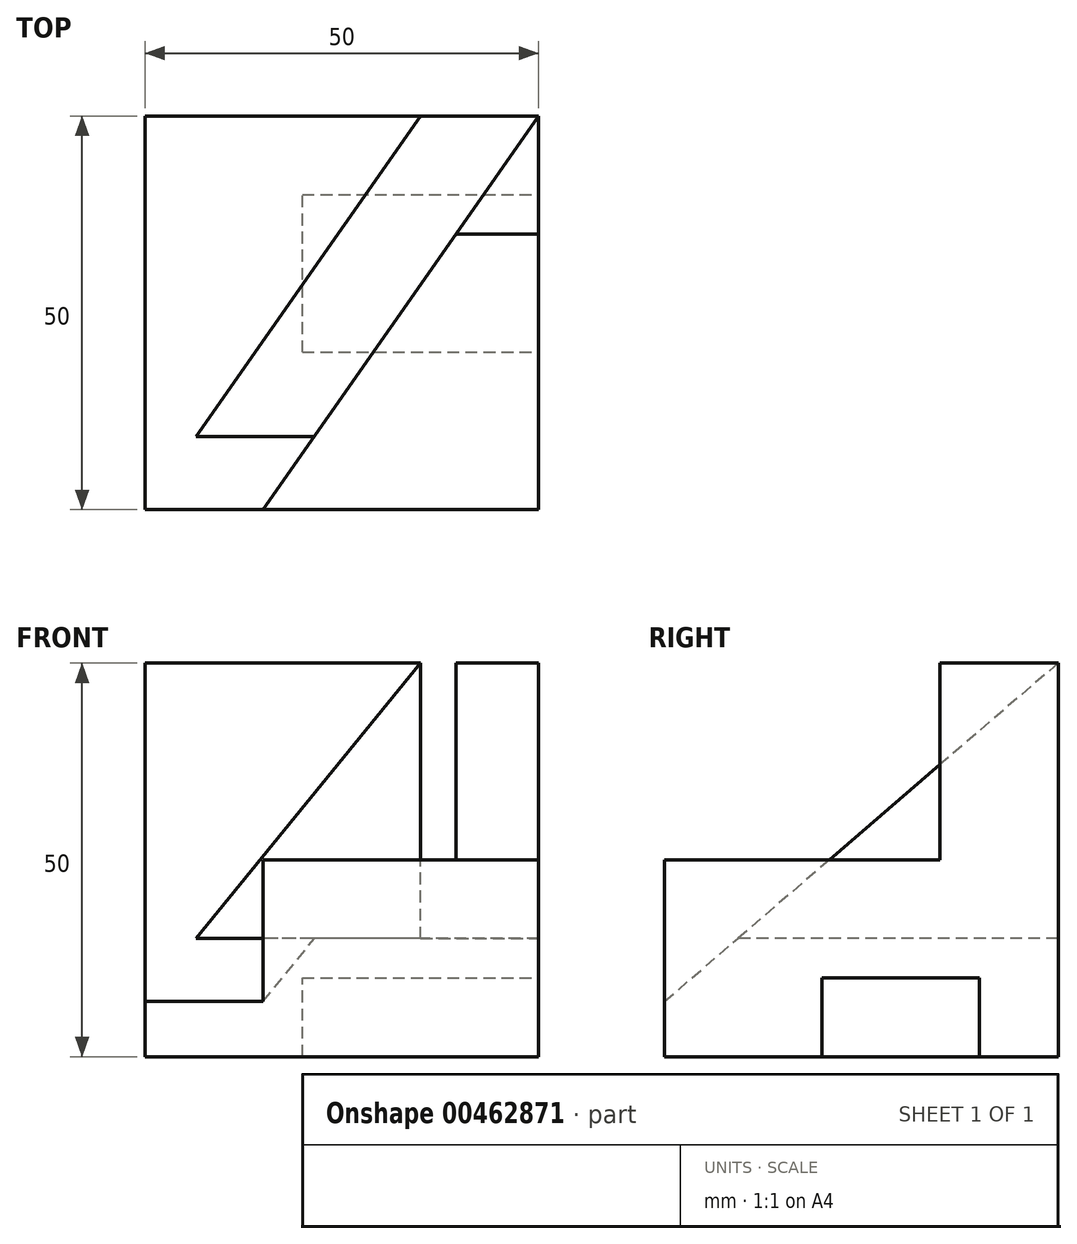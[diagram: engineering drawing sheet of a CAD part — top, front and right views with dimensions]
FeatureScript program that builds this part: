
annotation { "Feature Type Name" : "Feature", "Feature Type Description" : "" }
export const myFeature = defineFeature(function(context is Context, id is Id, definition is map)
    precondition{}
    {
        {
            var Q0;
            Q0=qCreatedBy(makeId("Top.planeOp"),FACE);
            var sketch = newSketch(context, id + "F0", { "sketchPlane" : qUnion([Q0])});
            skLineSegment(sketch, "E0.bottom", {"start": v(0, 0) * mm, "end": v(50, 0) * mm});
            skLineSegment(sketch, "E0.top", {"start": v(0, 50) * mm, "end": v(50, 50) * mm});
            skLineSegment(sketch, "E0.left", {"start": v(0, 0) * mm, "end": v(0, 50) * mm});
            skLineSegment(sketch, "E0.right", {"start": v(50, 0) * mm, "end": v(50, 50) * mm});
            skSolve(sketch);
        }
        {
            var Q0;
            Q0 = qSketchRegion(id + "F0", true);
            extrude(context, id + "F1", {"entities" : qUnion([Q0]), "depth" : 50 * mm});
        }
        {
            var Q0;
            Q0=makeQuery(id+"F1.opExtrude","SWEPT_FACE",FACE,{"disambiguationData":[OSD([sQuery(id+"F0.wireOp",EDGE,"E0.left")])]});
            var sketch = newSketch(context, id + "F2", { "sketchPlane" : qUnion([Q0])});
            skLineSegment(sketch, "E1", {"start": v(-50, 0) * mm, "end": v(-50, 7) * mm});
            skSolve(sketch);
        }
        {
            var Q0;
            Q0=makeQuery(id+"F1.opExtrude","SWEPT_FACE",FACE,{"disambiguationData":[OSD([sQuery(id+"F0.wireOp",EDGE,"E0.bottom")])]});
            var sketch = newSketch(context, id + "F3", { "sketchPlane" : qUnion([Q0])});
            skLineSegment(sketch, "E2", {"start": v(50, 0) * mm, "end": v(50, 7) * mm});
            skSolve(sketch);
        }
        {
            var Q0;
            {var subQ3=sQuery(id+"F3.wireOp",EDGE,"E2");Q0=makeQuery(id+"F3.imprint","IMPRINT",FACE,{"disambiguationData":[TD([[makeQuery(id+"F3.imprint","IMPRINT",EDGE,{"derivedFrom":subQ3}),-1.0]])]});}
            var sketch = newSketch(context, id + "F4", { "sketchPlane" : qUnion([Q0])});
            skLineSegment(sketch, "E3", {"start": v(0, 0) * mm, "end": v(0, 7) * mm});
            skSolve(sketch);
        }
        {
            var Q0;
            Q0=makeQuery(id+"F1.opExtrude","SWEPT_FACE",FACE,{"disambiguationData":[OSD([sQuery(id+"F0.wireOp",EDGE,"E0.right")])]});
            var sketch = newSketch(context, id + "F5", { "sketchPlane" : qUnion([Q0])});
            skLineSegment(sketch, "E4.bottom", {"start": v(20, 0) * mm, "end": v(40, 0) * mm});
            skLineSegment(sketch, "E4.top", {"start": v(20, 10) * mm, "end": v(40, 10) * mm});
            skLineSegment(sketch, "E4.left", {"start": v(20, 0) * mm, "end": v(20, 10) * mm});
            skLineSegment(sketch, "E4.right", {"start": v(40, 0) * mm, "end": v(40, 10) * mm});
            skSolve(sketch);
        }
        {
            var Q0;
            Q0 = qSketchRegion(id + "F5", true);
            extrude(context, id + "F6", {"entities" : qUnion([Q0]), "operationType" : NewBodyOperationType.REMOVE, "oppositeDirection" : true, "depth" : 30 * mm});
        }
        {
            var Q0;
            Q0=makeQuery(id+"F1.opExtrude","CAP_FACE",FACE,{"disambiguationData":[OSD([sQuery(id+"F0.wireOp",EDGE,"E0.bottom"),sQuery(id+"F0.wireOp",EDGE,"E0.top"),sQuery(id+"F0.wireOp",EDGE,"E0.left"),sQuery(id+"F0.wireOp",EDGE,"E0.right")])],"isStart":false});
            var sketch = newSketch(context, id + "F7", { "sketchPlane" : qUnion([Q0])});
            skLineSegment(sketch, "E5", {"start": v(50, 50) * mm, "end": v(35, 50) * mm});
            skLineSegment(sketch, "E6", {"start": v(50, 0) * mm, "end": v(15, 0) * mm});
            skLineSegment(sketch, "E7", {"start": v(50, 50) * mm, "end": v(15, 0) * mm});
            skLineSegment(sketch, "E8", {"start": v(35, 50) * mm, "end": v(0, 0) * mm});
            skSolve(sketch);
        }
        {
            var Q0;
            Q0 = qSketchRegion(id + "F7", true);
            var Q1;
            Q1=makeQuery(id+"F7.imprint","IMPRINT",FACE,{"disambiguationData":[TD([[makeQuery(id+"F7.imprint","IMPRINT",EDGE,{"derivedFrom":sQuery(id+"F7.wireOp",EDGE,"E5")}),-1.0]])]});
            extrude(context, id + "F8", {"entities" : qUnion([Q0, Q1]), "operationType" : NewBodyOperationType.REMOVE, "oppositeDirection" : true, "depth" : 35 * mm});
        }
        {
            var Q0;
            {var subQ0=sQuery(id+"F0.wireOp",EDGE,"E0.bottom");var subQ1=sQuery(id+"F0.wireOp",EDGE,"E0.right");Q0=makeQuery(id+"F8.boolean.opBoolean","SPLIT",FACE,{"disambiguationData":[TD([makeQuery(id+"F1.opExtrude","SWEPT_FACE",FACE,{"disambiguationData":[OSD([subQ0])]})])],"derivedFrom":makeQuery(id+"F1.opExtrude","CAP_FACE",FACE,{"disambiguationData":[OSD([subQ0,sQuery(id+"F0.wireOp",EDGE,"E0.top"),sQuery(id+"F0.wireOp",EDGE,"E0.left"),subQ1])],"isStart":false})});}
            var sketch = newSketch(context, id + "F9", { "sketchPlane" : qUnion([Q0])});
            skLineSegment(sketch, "E9", {"start": v(39.5, 35) * mm, "end": v(50, 35) * mm});
            skLineSegment(sketch, "E10", {"start": v(39.5, 35) * mm, "end": v(15, 0) * mm});
            skLineSegment(sketch, "E11", {"start": v(15, 0) * mm, "end": v(50, 0) * mm});
            skLineSegment(sketch, "E12", {"start": v(50, 0) * mm, "end": v(50, 35) * mm});
            skSolve(sketch);
        }
        {
            var Q0;
            Q0 = qSketchRegion(id + "F9", true);
            extrude(context, id + "F10", {"entities" : qUnion([Q0]), "operationType" : NewBodyOperationType.REMOVE, "oppositeDirection" : true, "depth" : 25 * mm});
        }
        {
            var Q0;
            {var subQ3=sQuery(id+"F2.wireOp",EDGE,"E1");Q0=makeQuery(id+"F2.imprint","IMPRINT",FACE,{"disambiguationData":[TD([[makeQuery(id+"F2.imprint","IMPRINT",EDGE,{"derivedFrom":subQ3}),1.0]])]});}
            var sketch = newSketch(context, id + "F11", { "sketchPlane" : qUnion([Q0])});
            skLineSegment(sketch, "E13", {"start": v(0, 50) * mm, "end": v(-50, 50) * mm});
            skLineSegment(sketch, "E14", {"start": v(-50, 50) * mm, "end": v(0, 7) * mm});
            skLineSegment(sketch, "E15", {"start": v(0, 7) * mm, "end": v(0, 50) * mm});
            skSolve(sketch);
        }
        {
            var Q0;
            Q0 = qSketchRegion(id + "F11", true);
            var Q1;
            Q1=makeQuery(id+"F8.boolean.opBoolean","COPY",FACE,{"derivedFrom":makeQuery(id+"F8.opExtrude","SWEPT_FACE",FACE,{"disambiguationData":[OSD([sQuery(id+"F7.wireOp",EDGE,"E7")])]})});
            extrude(context, id + "F12", {"entities" : qUnion([Q0]), "operationType" : NewBodyOperationType.REMOVE, "endBound" : BoundingType.UP_TO_SURFACE, "oppositeDirection" : true, "endBoundEntityFace" : qUnion([Q1]), "depth" : 25 * mm});
        }
    });
